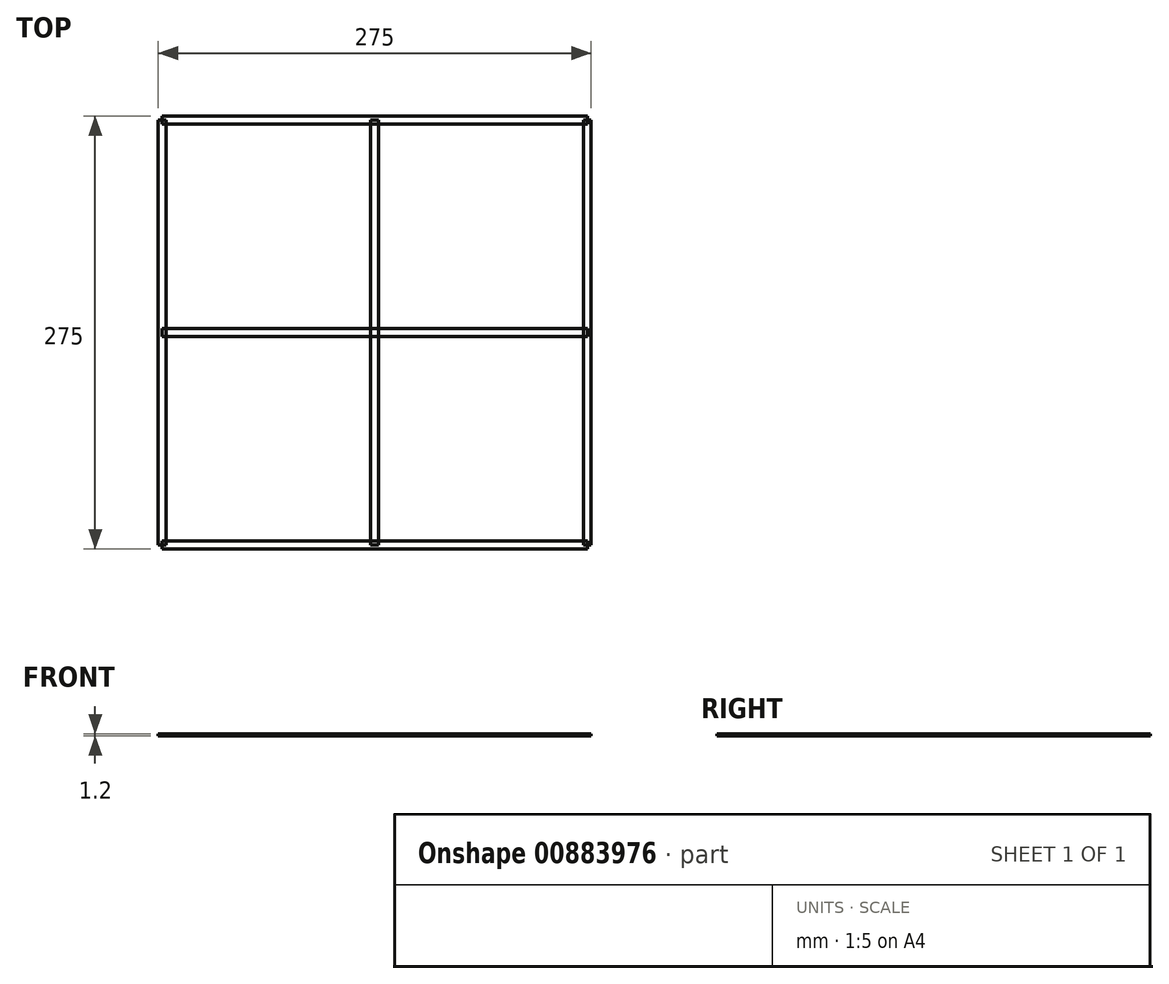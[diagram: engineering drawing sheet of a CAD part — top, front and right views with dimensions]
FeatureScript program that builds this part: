
annotation { "Feature Type Name" : "Feature", "Feature Type Description" : "" }
export const myFeature = defineFeature(function(context is Context, id is Id, definition is map)
    precondition{}
    {
        {
            var Q0;
            Q0=qCreatedBy(makeId("Top.planeOp"),FACE);
            var sketch = newSketch(context, id + "F0", { "sketchPlane" : qUnion([Q0])});
            skLineSegment(sketch, "E0.bottom", {"start": v(135, -2.5) * mm, "end": v(-135, -2.5) * mm});
            skLineSegment(sketch, "E0.top", {"start": v(135, 2.5) * mm, "end": v(-135, 2.5) * mm});
            skLineSegment(sketch, "E0.left", {"start": v(135, -2.5) * mm, "end": v(135, 2.5) * mm});
            skLineSegment(sketch, "E0.right", {"start": v(-135, -2.5) * mm, "end": v(-135, 2.5) * mm});
            skPoint(sketch, "E0.middle", {"position": v(0, 0) * mm});
            skLineSegment(sketch, "E1.bottom", {"start": v(2.5, -135) * mm, "end": v(-2.5, -135) * mm});
            skLineSegment(sketch, "E1.top", {"start": v(2.5, 135) * mm, "end": v(-2.5, 135) * mm});
            skLineSegment(sketch, "E1.left", {"start": v(2.5, -135) * mm, "end": v(2.5, 135) * mm});
            skLineSegment(sketch, "E1.right", {"start": v(-2.5, -135) * mm, "end": v(-2.5, 135) * mm});
            skLineSegment(sketch, "E2.bottom", {"start": v(-132.5, -135) * mm, "end": v(-137.5, -135) * mm});
            skLineSegment(sketch, "E2.top", {"start": v(-132.5, 135) * mm, "end": v(-137.5, 135) * mm});
            skLineSegment(sketch, "E2.left", {"start": v(-132.5, -135) * mm, "end": v(-132.5, 135) * mm});
            skLineSegment(sketch, "E2.right", {"start": v(-137.5, -135) * mm, "end": v(-137.5, 135) * mm});
            skPoint(sketch, "E2.middle", {"position": v(-135, 0) * mm});
            skLineSegment(sketch, "E3.bottom", {"start": v(135, 132.5) * mm, "end": v(-135, 132.5) * mm});
            skLineSegment(sketch, "E3.top", {"start": v(135, 137.5) * mm, "end": v(-135, 137.5) * mm});
            skLineSegment(sketch, "E3.left", {"start": v(135, 132.5) * mm, "end": v(135, 137.5) * mm});
            skLineSegment(sketch, "E3.right", {"start": v(-135, 132.5) * mm, "end": v(-135, 137.5) * mm});
            skPoint(sketch, "E3.middle", {"position": v(0, 135) * mm});
            skLineSegment(sketch, "E4.bottom", {"start": v(137.5, -135) * mm, "end": v(132.5, -135) * mm});
            skLineSegment(sketch, "E4.top", {"start": v(137.5, 135) * mm, "end": v(132.5, 135) * mm});
            skLineSegment(sketch, "E4.left", {"start": v(137.5, -135) * mm, "end": v(137.5, 135) * mm});
            skLineSegment(sketch, "E4.right", {"start": v(132.5, -135) * mm, "end": v(132.5, 135) * mm});
            skPoint(sketch, "E4.middle", {"position": v(135, 0) * mm});
            skLineSegment(sketch, "E5.bottom", {"start": v(135, -137.5) * mm, "end": v(-135, -137.5) * mm});
            skLineSegment(sketch, "E5.top", {"start": v(135, -132.5) * mm, "end": v(-135, -132.5) * mm});
            skLineSegment(sketch, "E5.left", {"start": v(135, -137.5) * mm, "end": v(135, -132.5) * mm});
            skLineSegment(sketch, "E5.right", {"start": v(-135, -137.5) * mm, "end": v(-135, -132.5) * mm});
            skPoint(sketch, "E5.middle", {"position": v(0, -135) * mm});
            skSolve(sketch);
        }
        {
            var Q0;
            {var subQ0=sQuery(id+"F0.wireOp",EDGE,"E3.left");var subQ1=sQuery(id+"F0.wireOp",EDGE,"E3.bottom");var subQ2=makeQuery(id+"F0.imprint","INTERSECT",VERTEX,{"derivedFrom":[subQ1,subQ0]});Q0=makeQuery(id+"F0.imprint","IMPRINT",FACE,{"disambiguationData":[TD([[makeQuery(id+"F0.imprint","IMPRINT",EDGE,{"disambiguationData":[TD([[subQ2,-1.0]])],"derivedFrom":subQ1}),-1.0]])]});}
            var Q1;
            {var subQ0=sQuery(id+"F0.wireOp",EDGE,"E2.left");var subQ1=sQuery(id+"F0.wireOp",EDGE,"E2.top");var subQ2=makeQuery(id+"F0.imprint","INTERSECT",VERTEX,{"derivedFrom":[subQ1,subQ0]});Q1=makeQuery(id+"F0.imprint","IMPRINT",FACE,{"disambiguationData":[TD([[makeQuery(id+"F0.imprint","IMPRINT",EDGE,{"disambiguationData":[TD([[subQ2,-1.0]])],"derivedFrom":subQ1}),1.0]])]});}
            var Q2;
            {var subQ0=sQuery(id+"F0.wireOp",EDGE,"E2.left");var subQ1=sQuery(id+"F0.wireOp",EDGE,"E2.bottom");var subQ2=makeQuery(id+"F0.imprint","INTERSECT",VERTEX,{"derivedFrom":[subQ1,subQ0]});Q2=makeQuery(id+"F0.imprint","IMPRINT",FACE,{"disambiguationData":[TD([[makeQuery(id+"F0.imprint","IMPRINT",EDGE,{"disambiguationData":[TD([[subQ2,-1.0]])],"derivedFrom":subQ1}),-1.0]])]});}
            var Q3;
            {var subQ0=sQuery(id+"F0.wireOp",EDGE,"E4.right");var subQ1=sQuery(id+"F0.wireOp",EDGE,"E4.bottom");var subQ2=makeQuery(id+"F0.imprint","INTERSECT",VERTEX,{"derivedFrom":[subQ1,subQ0]});Q3=makeQuery(id+"F0.imprint","IMPRINT",FACE,{"disambiguationData":[TD([[makeQuery(id+"F0.imprint","IMPRINT",EDGE,{"disambiguationData":[TD([[subQ2,1.0]])],"derivedFrom":subQ1}),-1.0]])]});}
            var Q4;
            {var subQ0=sQuery(id+"F0.wireOp",EDGE,"E1.bottom");Q4=makeQuery(id+"F0.imprint","IMPRINT",FACE,{"disambiguationData":[TD([[makeQuery(id+"F0.imprint","IMPRINT",EDGE,{"derivedFrom":subQ0}),-1.0]])]});}
            var Q5;
            {var subQ0=sQuery(id+"F0.wireOp",EDGE,"E0.left");Q5=makeQuery(id+"F0.imprint","IMPRINT",FACE,{"disambiguationData":[TD([[makeQuery(id+"F0.imprint","IMPRINT",EDGE,{"derivedFrom":subQ0}),1.0]])]});}
            var Q6;
            {var subQ0=sQuery(id+"F0.wireOp",EDGE,"E0.right");Q6=makeQuery(id+"F0.imprint","IMPRINT",FACE,{"disambiguationData":[TD([[makeQuery(id+"F0.imprint","IMPRINT",EDGE,{"derivedFrom":subQ0}),-1.0]])]});}
            var Q7;
            {var subQ0=sQuery(id+"F0.wireOp",EDGE,"E1.top");Q7=makeQuery(id+"F0.imprint","IMPRINT",FACE,{"disambiguationData":[TD([[makeQuery(id+"F0.imprint","IMPRINT",EDGE,{"derivedFrom":subQ0}),1.0]])]});}
            extrude(context, id + "F1", {"entities" : qUnion([Q0, Q1, Q2, Q3, Q4, Q5, Q6, Q7]), "depth" : 1.2 * mm, "offsetDistance" : 25 * mm});
        }
        {
            var Q0;
            {var subQ12=sQuery(id+"F0.wireOp",EDGE,"E0.right");Q0=makeQuery(id+"F0.imprint","IMPRINT",FACE,{"disambiguationData":[TD([[makeQuery(id+"F0.imprint","IMPRINT",EDGE,{"derivedFrom":subQ12}),1.0]])]});}
            var Q1;
            {var subQ0=sQuery(id+"F0.wireOp",EDGE,"E1.right");var subQ1=sQuery(id+"F0.wireOp",EDGE,"E0.bottom");var subQ2=makeQuery(id+"F0.imprint","INTERSECT",VERTEX,{"derivedFrom":[subQ1,subQ0]});Q1=makeQuery(id+"F0.imprint","IMPRINT",FACE,{"disambiguationData":[TD([[makeQuery(id+"F0.imprint","IMPRINT",EDGE,{"disambiguationData":[TD([[subQ2,-1.0]])],"derivedFrom":subQ1}),-1.0]])]});}
            var Q2;
            {var subQ0=sQuery(id+"F0.wireOp",EDGE,"E1.left");var subQ1=sQuery(id+"F0.wireOp",EDGE,"E0.top");var subQ2=makeQuery(id+"F0.imprint","INTERSECT",VERTEX,{"derivedFrom":[subQ1,subQ0]});Q2=makeQuery(id+"F0.imprint","IMPRINT",FACE,{"disambiguationData":[TD([[makeQuery(id+"F0.imprint","IMPRINT",EDGE,{"disambiguationData":[TD([[subQ2,-1.0]])],"derivedFrom":subQ1}),-1.0]])]});}
            var Q3;
            {var subQ5=sQuery(id+"F0.wireOp",EDGE,"E1.top");Q3=makeQuery(id+"F0.imprint","IMPRINT",FACE,{"disambiguationData":[TD([[makeQuery(id+"F0.imprint","IMPRINT",EDGE,{"derivedFrom":subQ5}),-1.0]])]});}
            var Q4;
            {var subQ13=sQuery(id+"F0.wireOp",EDGE,"E0.left");Q4=makeQuery(id+"F0.imprint","IMPRINT",FACE,{"disambiguationData":[TD([[makeQuery(id+"F0.imprint","IMPRINT",EDGE,{"derivedFrom":subQ13}),-1.0]])]});}
            var Q5;
            {var subQ14=sQuery(id+"F0.wireOp",EDGE,"E1.bottom");Q5=makeQuery(id+"F0.imprint","IMPRINT",FACE,{"disambiguationData":[TD([[makeQuery(id+"F0.imprint","IMPRINT",EDGE,{"derivedFrom":subQ14}),1.0]])]});}
            var Q6;
            {var subQ0=sQuery(id+"F0.wireOp",EDGE,"E4.right");var subQ1=sQuery(id+"F0.wireOp",EDGE,"E0.bottom");var subQ2=makeQuery(id+"F0.imprint","INTERSECT",VERTEX,{"derivedFrom":[subQ1,subQ0]});Q6=makeQuery(id+"F0.imprint","IMPRINT",FACE,{"disambiguationData":[TD([[makeQuery(id+"F0.imprint","IMPRINT",EDGE,{"disambiguationData":[TD([[subQ2,-1.0]])],"derivedFrom":subQ1}),-1.0]])]});}
            var Q7;
            {var subQ0=sQuery(id+"F0.wireOp",EDGE,"E1.left");var subQ1=sQuery(id+"F0.wireOp",EDGE,"E0.bottom");var subQ2=makeQuery(id+"F0.imprint","INTERSECT",VERTEX,{"derivedFrom":[subQ1,subQ0]});Q7=makeQuery(id+"F0.imprint","IMPRINT",FACE,{"disambiguationData":[TD([[makeQuery(id+"F0.imprint","IMPRINT",EDGE,{"disambiguationData":[TD([[subQ2,-1.0]])],"derivedFrom":subQ1}),1.0]])]});}
            extrude(context, id + "F2", {"entities" : qUnion([Q0, Q1, Q2, Q3, Q4, Q5, Q6, Q7]), "depth" : 1.2 * mm, "offsetDistance" : 25 * mm});
        }
    });
